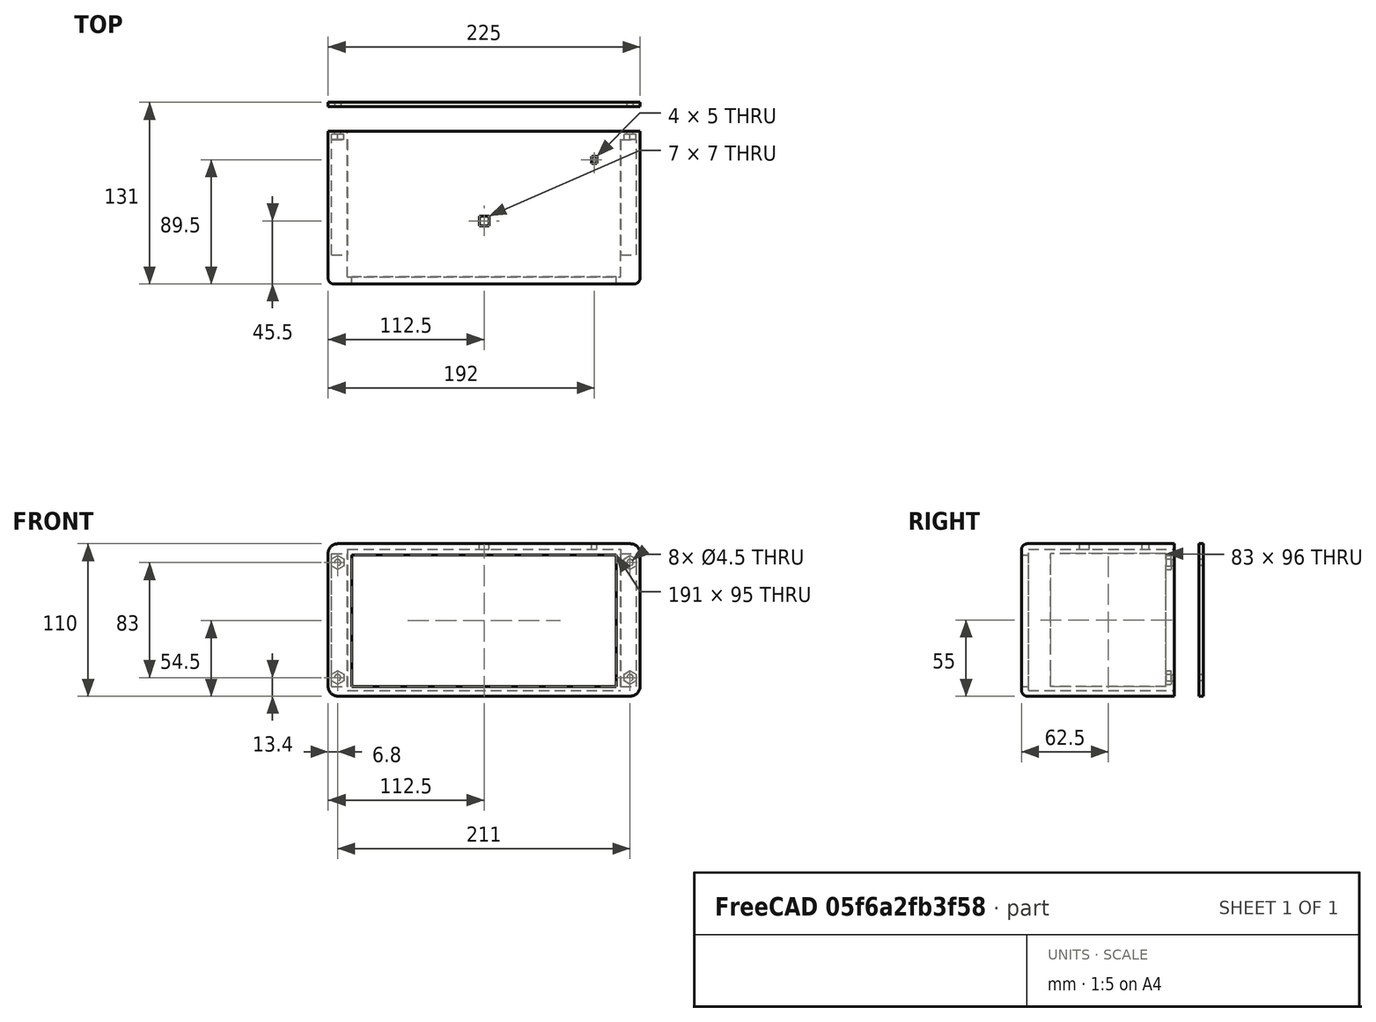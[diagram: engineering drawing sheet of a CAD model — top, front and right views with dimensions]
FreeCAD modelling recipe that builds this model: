
FCSTD DOCUMENT  (FreeCAD 0.18R4 (GitTag))
Label: CADBacking
License: All rights reserved
LicenseURL: http://en.wikipedia.org/wiki/All_rights_reserved
objects: Part::Cut×10, Part::Cylinder×8, Part::Box×7, Part::Fuse×7, Part::Prism×4, Part::Fillet×2
note: 38 computed .brp shape members not serialized (recipe doc carries the construction recipe); baked Part::Feature solids carry a one-line shape summary decoded from their .brp

FEATURE [Part::Box] Box  label="Cube"
  AttacherType = Attacher::AttachEngine3D
  Height = 110
  Length = 225
  Width = 3
FEATURE [Part::Fillet] Fillet
  Base = -> Box
  Edges = 4 edges r=7: [Edge2,Edge4,Edge6,Edge8]
FEATURE [Part::Cylinder] Cylinder
  Angle = 360
  AttacherType = Attacher::AttachEngine3D
  Height = 3
  Placement = pos=(6.8,-18,13.4) rot=(1,0,0;1.5708rad)
  Radius = 2.25
FEATURE [Part::Cylinder] Cylinder001
  Angle = 360
  AttacherType = Attacher::AttachEngine3D
  Height = 2
  Placement = pos=(6.8,158,13.4) rot=(-1,0,0;1.5708rad)
  Radius = 2.25
FEATURE [Part::Prism] Prism001
  AttacherType = Attacher::AttachEngine3D
  Circumradius = 5
  Height = 4
  Placement = pos=(6.83013,154,13.4378) rot=(-0.935113,0.250563,0.250563;1.63783rad)
  Polygon = 6
FEATURE [Part::Cylinder] Cylinder003
  Angle = 360
  AttacherType = Attacher::AttachEngine3D
  Height = 2
  Placement = pos=(6.8,158,13.4) rot=(-1,0,0;1.5708rad)
  Radius = 2.25
FEATURE [Part::Cylinder] Cylinder004
  Angle = 360
  AttacherType = Attacher::AttachEngine3D
  Height = 2
  Placement = pos=(6.8,158,13.4) rot=(-1,0,0;1.5708rad)
  Radius = 2.25
FEATURE [Part::Prism] Prism003
  AttacherType = Attacher::AttachEngine3D
  Circumradius = 5
  Height = 4
  Placement = pos=(6.83013,154,13.4378) rot=(-0.935113,0.250563,0.250563;1.63783rad)
  Polygon = 6
FEATURE [Part::Cylinder] Cylinder002
  Angle = 360
  AttacherType = Attacher::AttachEngine3D
  Height = 2
  Placement = pos=(6.8,158,13.4) rot=(-1,0,0;1.5708rad)
  Radius = 2.25
FEATURE [Part::Prism] Prism002
  AttacherType = Attacher::AttachEngine3D
  Circumradius = 5
  Height = 4
  Placement = pos=(6.83013,154,13.4378) rot=(-0.935113,0.250563,0.250563;1.63783rad)
  Polygon = 6
FEATURE [Part::Box] Box007  label="Outer Cube"
  AttacherType = Attacher::AttachEngine3D
  Height = 110
  Length = 225
  Width = 110
FEATURE [Part::Prism] Prism
  AttacherType = Attacher::AttachEngine3D
  Circumradius = 5
  Height = 4
  Placement = pos=(6.83013,154,13.4378) rot=(-0.935113,0.250563,0.250563;1.63783rad)
  Polygon = 6
FEATURE [Part::Fillet] Fillet001
  Base = -> Box007
  Edges = 8 edges: [Edge1 r=4,Edge2 r=7,Edge4 r=7,Edge5 r=4,Edge6 r=7,Edge8 r=7,Edge9 r=4,Edge10 r=4]
FEATURE [Part::Box] Box003  label="Inner Cube 2"
  AttacherType = Attacher::AttachEngine3D
  Height = 95
  Length = 191
  Placement = pos=(17,-3,7) rot=(0,0,1;0rad)
  Width = 50
FEATURE [Part::Cylinder] Cylinder005
  Angle = 360
  AttacherType = Attacher::AttachEngine3D
  Height = 3
  Placement = pos=(6.8,-18,96.4) rot=(1,0,0;1.5708rad)
  Radius = 2.25
FEATURE [Part::Cylinder] Cylinder006
  Angle = 360
  AttacherType = Attacher::AttachEngine3D
  Height = 3
  Placement = pos=(217.8,-18,96.4) rot=(1,0,0;1.5708rad)
  Radius = 2.25
FEATURE [Part::Cylinder] Cylinder007
  Angle = 360
  AttacherType = Attacher::AttachEngine3D
  Height = 3
  Placement = pos=(217.8,-18,13.4) rot=(1,0,0;1.5708rad)
  Radius = 2.25
FEATURE [Part::Fuse] Fusion  label="Bottom left Bolt"
  Base = -> Prism
  Placement = pos=(0,-50,0) rot=(0,0,1;0rad)
  Tool = -> Cylinder004
FEATURE [Part::Fuse] Fusion002  label="Bottom Right Bolt"
  Base = -> Prism002
  Placement = pos=(211,-50,0) rot=(0,0,1;0rad)
  Tool = -> Cylinder002
FEATURE [Part::Box] Box005  label="LightSensor"
  AttacherType = Attacher::AttachEngine3D
  Height = 4
  Length = 4
  Placement = pos=(190,87,106) rot=(0,0,1;0rad)
  Width = 5
FEATURE [Part::Cut] Cut
  Base = -> Fillet001
  Tool = -> Box003
FEATURE [Part::Fuse] Fusion001  label="Top Left Bolt"
  Base = -> Prism001
  Placement = pos=(0,-50,83) rot=(0,0,1;0rad)
  Tool = -> Cylinder001
FEATURE [Part::Fuse] Fusion003  label="Top Right Bolt"
  Base = -> Prism003
  Placement = pos=(211,-50,83) rot=(0,0,1;0rad)
  Tool = -> Cylinder003
FEATURE [Part::Box] Box002  label="Inner Cube 1"
  AttacherType = Attacher::AttachEngine3D
  Height = 102
  Length = 197
  Placement = pos=(14,5,4) rot=(0,0,1;0rad)
  Width = 108
FEATURE [Part::Cut] Cut001
  Base = -> Cut
  Tool = -> Box002
FEATURE [Part::Box] Box006  label="Button"
  AttacherType = Attacher::AttachEngine3D
  Height = 4
  Length = 7
  Placement = pos=(109,42,106) rot=(0,0,1;0rad)
  Width = 7
FEATURE [Part::Box] Box004  label="BoltCuttout"
  AttacherType = Attacher::AttachEngine3D
  Height = 96
  Length = 220
  Placement = pos=(2.5,21,7) rot=(0,0,1;0rad)
  Width = 83
FEATURE [Part::Cut] Cut002
  Base = -> Cut001
  Tool = -> Box004
FEATURE [Part::Cut] Cut003
  Base = -> Cut002
  Tool = -> Fusion
FEATURE [Part::Cut] Cut004
  Base = -> Cut003
  Tool = -> Fusion001
FEATURE [Part::Cut] Cut005
  Base = -> Cut004
  Tool = -> Fusion003
FEATURE [Part::Cut] Cut006
  Base = -> Cut005
  Tool = -> Fusion002
FEATURE [Part::Cut] Cut007
  Base = -> Cut006
  Tool = -> Box005
FEATURE [Part::Cut] Cut008
  Base = -> Cut007
  Placement = pos=(0,-128,0) rot=(0,0,1;0rad)
  Tool = -> Box006
FEATURE [Part::Fuse] Fusion004
  Base = -> Cylinder
  Tool = -> Cylinder005
FEATURE [Part::Fuse] Fusion005
  Base = -> Cylinder006
  Tool = -> Cylinder007
FEATURE [Part::Fuse] Fusion006  label="Screw Holes"
  Base = -> Fusion004
  Placement = pos=(0,21,0) rot=(0,0,1;0rad)
  Tool = -> Fusion005
FEATURE [Part::Cut] Cut009
  Base = -> Fillet
  Tool = -> Fusion006
